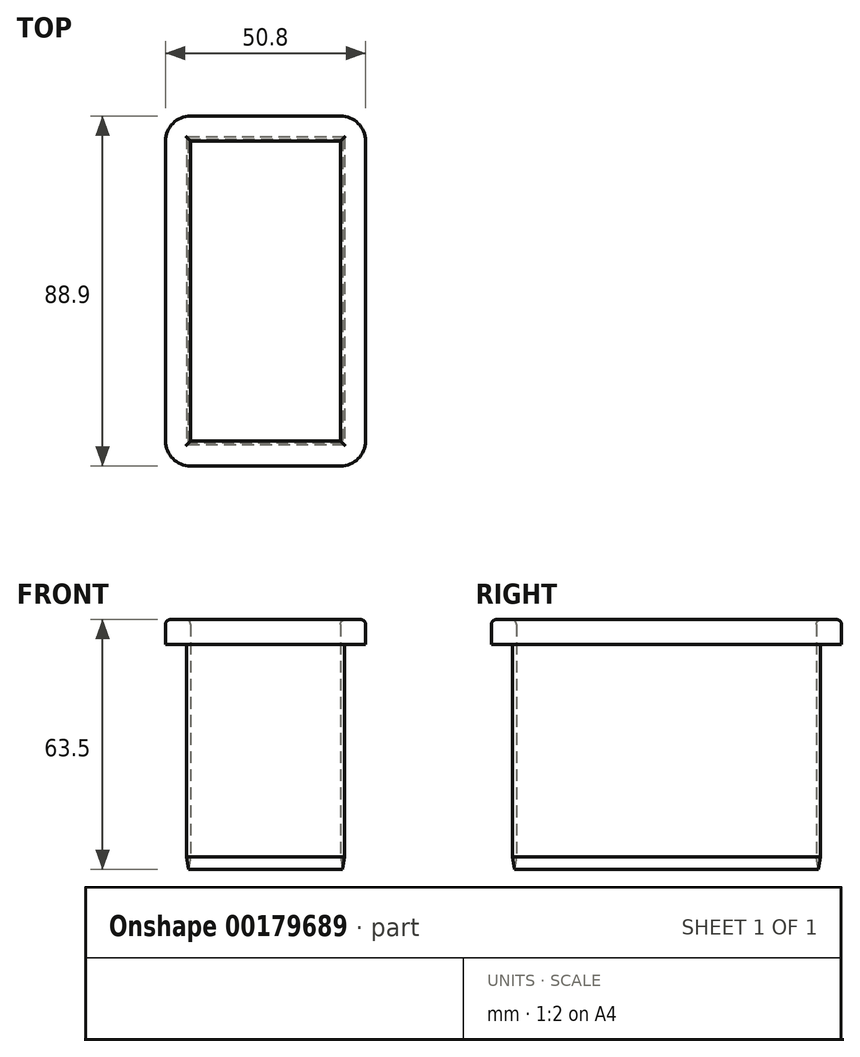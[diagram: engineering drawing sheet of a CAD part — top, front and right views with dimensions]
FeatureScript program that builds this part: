
annotation { "Feature Type Name" : "Feature", "Feature Type Description" : "" }
export const myFeature = defineFeature(function(context is Context, id is Id, definition is map)
    precondition{}
    {
        {
            var Q0;
            Q0=qCreatedBy(makeId("Top.planeOp"),FACE);
            var sketch = newSketch(context, id + "F0", { "sketchPlane" : qUnion([Q0])});
            skLineSegment(sketch, "E0.bottom", {"start": v(19.05, 38.1) * mm, "end": v(-19.05, 38.1) * mm});
            skLineSegment(sketch, "E0.top", {"start": v(19.05, -38.1) * mm, "end": v(-19.05, -38.1) * mm});
            skLineSegment(sketch, "E0.left", {"start": v(19.05, 38.1) * mm, "end": v(19.05, -38.1) * mm});
            skLineSegment(sketch, "E0.right", {"start": v(-19.05, 38.1) * mm, "end": v(-19.05, -38.1) * mm});
            skPoint(sketch, "E0.middle", {"position": v(0, 0) * mm});
            skLineSegment(sketch, "E1.bottom", {"start": v(19.05, 44.45) * mm, "end": v(-19.05, 44.45) * mm});
            skLineSegment(sketch, "E1.top", {"start": v(19.05, -44.45) * mm, "end": v(-19.05, -44.45) * mm});
            skLineSegment(sketch, "E1.left", {"start": v(25.4, 38.1) * mm, "end": v(25.4, -38.1) * mm});
            skLineSegment(sketch, "E1.right", {"start": v(-25.4, 38.1) * mm, "end": v(-25.4, -38.1) * mm});
            skLineSegment(sketch, "E2", {"start": v(19.05, 0) * mm, "end": v(25.4, 0) * mm, "construction": true});
            skLineSegment(sketch, "E3", {"start": v(0, -38.1) * mm, "end": v(0, -44.45) * mm, "construction": true});
            skLineSegment(sketch, "E4.bottom", {"start": v(20.05, 39.1) * mm, "end": v(-20.05, 39.1) * mm});
            skLineSegment(sketch, "E4.top", {"start": v(20.05, -39.1) * mm, "end": v(-20.05, -39.1) * mm});
            skLineSegment(sketch, "E4.left", {"start": v(20.05, 39.1) * mm, "end": v(20.05, -39.1) * mm});
            skLineSegment(sketch, "E4.right", {"start": v(-20.05, 39.1) * mm, "end": v(-20.05, -39.1) * mm});
            skLineSegment(sketch, "E5", {"start": v(0, 38.1) * mm, "end": v(0, 39.1) * mm, "construction": true});
            skLineSegment(sketch, "E6", {"start": v(-19.05, 0) * mm, "end": v(-20.05, 0) * mm, "construction": true});
            skPoint(sketch, "E7.visualSharp", {"position": v(-25.4, 44.45) * mm});
            skArc(sketch, "E7.filletArc", {"start": v(-19.05, 44.45) * mm, "mid": v(-23.54, 42.6) * mm, "end": v(-25.4, 38.1) * mm});
            skPoint(sketch, "E8.visualSharp", {"position": v(25.4, 44.45) * mm});
            skArc(sketch, "E8.filletArc", {"start": v(25.4, 38.1) * mm, "mid": v(23.54, 42.6) * mm, "end": v(19.05, 44.45) * mm});
            skPoint(sketch, "E9.visualSharp", {"position": v(25.4, -44.45) * mm});
            skArc(sketch, "E9.filletArc", {"start": v(19.05, -44.45) * mm, "mid": v(23.54, -42.6) * mm, "end": v(25.4, -38.1) * mm});
            skPoint(sketch, "E10.visualSharp", {"position": v(-25.4, -44.45) * mm});
            skArc(sketch, "E10.filletArc", {"start": v(-25.4, -38.1) * mm, "mid": v(-23.54, -42.6) * mm, "end": v(-19.05, -44.45) * mm});
            skSolve(sketch);
        }
        {
            var Q0;
            Q0 = qSketchRegion(id + "F0", true);
            var Q1;
            Q1=makeQuery(id+"F0.imprint","IMPRINT",FACE,{"disambiguationData":[TD([[makeQuery(id+"F0.imprint","IMPRINT",EDGE,{"derivedFrom":sQuery(id+"F0.wireOp",EDGE,"E0.bottom")}),-1.0]])]});
            extrude(context, id + "F1", {"entities" : qUnion([Q0, Q1]), "depth" : 6.35 * mm});
        }
        {
            var Q0;
            Q0=makeQuery(id+"F1.opExtrude","CAP_FACE",FACE,{"disambiguationData":[OSD([sQuery(id+"F0.wireOp",EDGE,"E0.bottom"),sQuery(id+"F0.wireOp",EDGE,"E0.top"),sQuery(id+"F0.wireOp",EDGE,"E0.left"),sQuery(id+"F0.wireOp",EDGE,"E0.right"),sQuery(id+"F0.wireOp",EDGE,"E1.bottom"),sQuery(id+"F0.wireOp",EDGE,"E1.top"),sQuery(id+"F0.wireOp",EDGE,"E1.left"),sQuery(id+"F0.wireOp",EDGE,"E1.right"),sQuery(id+"F0.wireOp",EDGE,"E7.filletArc"),sQuery(id+"F0.wireOp",EDGE,"E8.filletArc"),sQuery(id+"F0.wireOp",EDGE,"E9.filletArc"),sQuery(id+"F0.wireOp",EDGE,"E10.filletArc")])],"isStart":true});
            var sketch = newSketch(context, id + "F2", { "sketchPlane" : qUnion([Q0])});
            skLineSegment(sketch, "E11.0", {"start": v(-20.05, -39.1) * mm, "end": v(-20.05, 39.1) * mm});
            skLineSegment(sketch, "E11.1", {"start": v(20.05, -39.1) * mm, "end": v(-20.05, -39.1) * mm});
            skLineSegment(sketch, "E11.2", {"start": v(20.05, -39.1) * mm, "end": v(20.05, 39.1) * mm});
            skLineSegment(sketch, "E11.3", {"start": v(20.05, 39.1) * mm, "end": v(-20.05, 39.1) * mm});
            skLineSegment(sketch, "E11.4", {"start": v(19.05, 38.1) * mm, "end": v(-19.05, 38.1) * mm});
            skLineSegment(sketch, "E11.5", {"start": v(19.05, -38.1) * mm, "end": v(19.05, 38.1) * mm});
            skLineSegment(sketch, "E11.6", {"start": v(19.05, -38.1) * mm, "end": v(-19.05, -38.1) * mm});
            skLineSegment(sketch, "E11.7", {"start": v(-19.05, -38.1) * mm, "end": v(-19.05, 38.1) * mm});
            skSolve(sketch);
        }
        {
            var Q0;
            Q0 = qSketchRegion(id + "F2", true);
            extrude(context, id + "F3", {"entities" : qUnion([Q0]), "operationType" : NewBodyOperationType.ADD, "depth" : 57.15 * mm});
        }
        {
            var Q0;
            Q0=makeQuery(id+"F3.opExtrude","CAP_FACE",FACE,{"disambiguationData":[OSD([sQuery(id+"F2.wireOp",EDGE,"E11.0"),sQuery(id+"F2.wireOp",EDGE,"E11.1"),sQuery(id+"F2.wireOp",EDGE,"E11.2"),sQuery(id+"F2.wireOp",EDGE,"E11.3"),sQuery(id+"F2.wireOp",EDGE,"E11.4"),sQuery(id+"F2.wireOp",EDGE,"E11.5"),sQuery(id+"F2.wireOp",EDGE,"E11.6"),sQuery(id+"F2.wireOp",EDGE,"E11.7")])],"isStart":false});
            chamfer(context, id + "F4", {"entities" : qUnion([Q0]), "chamferType" : ChamferType.TWO_OFFSETS, "width1" : 3.17 * mm, "oppositeDirection" : false, "width2" : .5 * mm, "tangentPropagation" : true});
        }
        {
            var Q0;
            Q0=makeQuery(id+"F1.opExtrude","CAP_FACE",FACE,{"disambiguationData":[OSD([sQuery(id+"F0.wireOp",EDGE,"E0.bottom"),sQuery(id+"F0.wireOp",EDGE,"E0.top"),sQuery(id+"F0.wireOp",EDGE,"E0.left"),sQuery(id+"F0.wireOp",EDGE,"E0.right"),sQuery(id+"F0.wireOp",EDGE,"E1.bottom"),sQuery(id+"F0.wireOp",EDGE,"E1.top"),sQuery(id+"F0.wireOp",EDGE,"E1.left"),sQuery(id+"F0.wireOp",EDGE,"E1.right"),sQuery(id+"F0.wireOp",EDGE,"E7.filletArc"),sQuery(id+"F0.wireOp",EDGE,"E8.filletArc"),sQuery(id+"F0.wireOp",EDGE,"E9.filletArc"),sQuery(id+"F0.wireOp",EDGE,"E10.filletArc")])],"isStart":false});
            fillet(context, id + "F5", {"entities" : qUnion([Q0]), "radius" : 1.27 * mm, "tangentPropagation" : true, "allowEdgeOverflow" : false});
        }
    });
